# Revit family: Electronics_Paging-Stations_Biamp_Tesira_NPX-G1040_G1100__
name_source: partatom
category: Communication Devices
units: mm (PartAtom-declared; Revit-internal decimal feet)

## family parameters
Cut with Voids When Loaded = No
Host = Face
Maintain Annotation Orientation = No
OmniClass Number = 23.85.10.11.14
OmniClass Title = Audio Equipment
Part Type = Normal
Room Calculation Point = No
Round Connector Dimension = Use Diameter
Shared = No

## types (2) — shared parameters
Altitude = 0-10,000 ft (0-3000m) MSL
Apparent Load = 0 VA
Compliance = FCC Part 15B (USA); CE marked (Europe); NRTL listed to UL 62638-1 (USA); NRTL listed to CSA C22.2 #62368-1 (Canada); RoHS Directive (Europe)
Connector Description = PoE+ (IEEE 802.3at Class 3, 15.4W)
Default Elevation = 48 "
Depth = 7.2 "
Dynamic Range = 92dB, A-Weighted THD+N < 1%
Frequency Response = ± 3dB at 150Hz - 16kHz
Height = 1.9 "
Housing Material = Biamp - Plastic - Black
Humidity = 0-95% relative humidity (non-condensing)
Manufacturer = Biamp
Max Power Consumption = 0 W
Maximum SPL = 109dB THD+N < 1%
Mic Gooseneck Length = 13.5 "
Mic Pattern = Cardioid
Mic Type = MEMS
Network Connection = Gigabit Ethernet, RJ-45 (Cat 5e and above)
Number of Poles = 1
Power Factor = 1
Product Documentation Link = https://downloads.biamp.com
Product Page URL = https://www.biamp.com
Product data url = https://www.bimobject.com
SNR = > 76dB at 1kHz, 94dBSPL A-Weighted
Temperature Range = 32 - 104° F (0 - 40° C)
URL = https://www.biamp.com
Voltage = 0 V
Weight = 2.40 lbf
Width = 9.1 "

## per-type parameters (varying)
| type | Description | G1040 | Model |
| G1040 | NPX G1040 Convenience Paging Station | Yes | NPX G1040 |
| G1100 | NPX G1100 Convenience Paging Station | No | NPX G1100 |

## geometry (parser evidence)
native form markers: Sweep x2
no freeform markers — native parametric forms only
